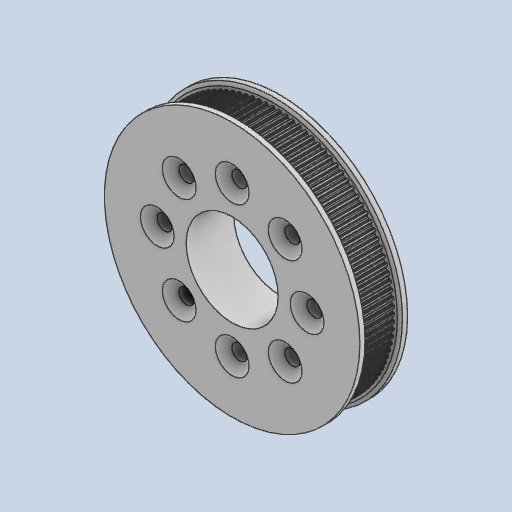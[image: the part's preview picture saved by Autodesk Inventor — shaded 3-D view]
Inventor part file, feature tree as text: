
AUTODESK INVENTOR PART (.ipt)
format: ipt  version: 2024 (Build 280153000, 153)  size: 3,526,144 bytes
history: native  units: mm
features: extrude x4, sketch x3, chamfer x2, projected_geometry x2, pattern_circular x1, mirror x1
ambient origin geometry x8: Origin, YZ Plane, XZ Plane, XY Plane, X Axis, Y Axis, Z Axis, Center Point
bodies: Solid1 (feature_tree)
feature tree (13):
  extrude  "Extrusion1"  Depth=0.277778mm
  pattern_circular  "Circular Pattern1"  [2 undecoded]
  extrude  "Extrusion2"  Depth=0.555mm
  chamfer  "Chamfer1"  Distance=1.0mm
  mirror  "Mirror1"
  extrude  "Extrusion5"  Depth=0.15mm
  extrude  "Extrusion6"  Depth=0.6mm
  chamfer  "Chamfer2"  Distance=10.0mm
  sketch  "Sketch1"  dims[d0=72.0mm d1=0.277778mm]
  sketch  "Sketch6"  dims[d2=0.111111mm]
  projected_geometry  "Projected Loop2"
  sketch  "Sketch7"  dims[d3=1.004mm d4=0.75mm d5=0.555mm d6=1.0mm d7=0.15mm d9=0.6mm d10=10.0mm d11=0.0mm d12=1130.973355mm d13=360.0deg d15=75.0mm d16=2.0mm d17=0.0mm d18=1.0mm d19=0.5mm d20=45.0deg d21=5.0mm d31=27.0mm d32=0.0mm d33=0.0mm d34=22.0mm d35=4.5mm d36=80.0mm d38=360.0deg d40=0.0mm d41=0.0mm d42=2.7mm d43=2.2mm d44=45.0deg]
  projected_geometry  "Projected Loop3"
note: 2 required parameter values undecoded (feature->parameter linkage not recoverable at this tier; creation-order binding heuristic only, values carry confidence <= 0.55)
